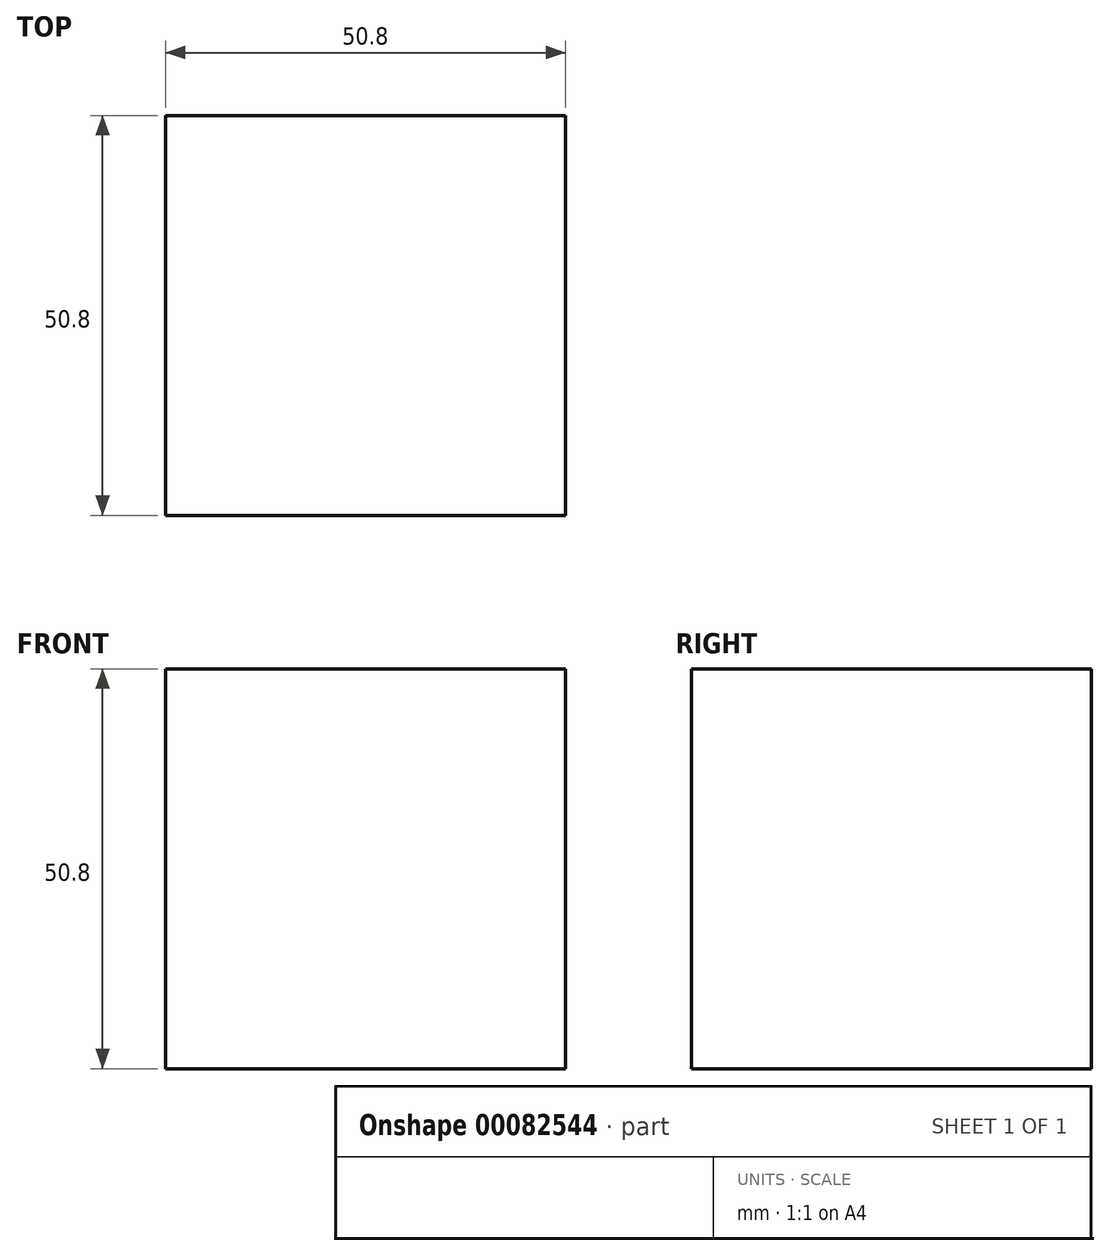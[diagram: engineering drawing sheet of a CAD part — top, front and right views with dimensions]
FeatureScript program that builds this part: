
annotation { "Feature Type Name" : "Feature", "Feature Type Description" : "" }
export const myFeature = defineFeature(function(context is Context, id is Id, definition is map)
    precondition{}
    {
        {
            var Q0;
            Q0=qCreatedBy(makeId("Front.planeOp"),FACE);
            var sketch = newSketch(context, id + "F0", { "sketchPlane" : qUnion([Q0])});
            skLineSegment(sketch, "E0.bottom", {"start": v(25.4, -25.4) * mm, "end": v(-25.4, -25.4) * mm});
            skLineSegment(sketch, "E0.top", {"start": v(25.4, 25.4) * mm, "end": v(-25.4, 25.4) * mm});
            skLineSegment(sketch, "E0.left", {"start": v(25.4, -25.4) * mm, "end": v(25.4, 25.4) * mm});
            skLineSegment(sketch, "E0.right", {"start": v(-25.4, -25.4) * mm, "end": v(-25.4, 25.4) * mm});
            skPoint(sketch, "E0.middle", {"position": v(0, 0) * mm});
            skSolve(sketch);
        }
        {
            var Q0;
            Q0=makeQuery(id+"F0.imprint","IMPRINT",FACE,{"disambiguationData":[TD([[makeQuery(id+"F0.imprint","IMPRINT",EDGE,{"derivedFrom":sQuery(id+"F0.wireOp",EDGE,"E0.bottom")}),-1.0]])]});
            extrude(context, id + "F1", {"entities" : qUnion([Q0]), "endBound" : BoundingType.SYMMETRIC, "depth" : 50.8 * mm});
        }
    });
